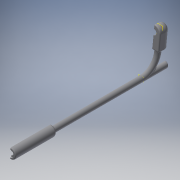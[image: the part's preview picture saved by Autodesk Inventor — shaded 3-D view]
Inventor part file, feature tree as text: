
AUTODESK INVENTOR PART (.ipt)
format: ipt  version: 2018 (Build 220112000, 112)  size: 352,256 bytes
history: native  units: mm
features: sketch x9, extrude x7, fillet x5, projected_geometry x3, plane x2, revolve x1, sweep x1
ambient origin geometry x8: Origin, YZ Plane, XZ Plane, XY Plane, X Axis, Y Axis, Z Axis, Center Point
bodies: Solid1 (feature_tree)
feature tree (28):
  revolve  "Revolution1"  [1 undecoded]
  fillet  "Fillet1"  Radius=8.0mm
  fillet  "Fillet2"  Radius=40.0mm
  fillet  "Fillet3"  [1 undecoded]
  plane  "Work Plane1"
  sweep  "Sweep1"
  extrude  "Extrusion2"  Depth=1.5mm
  fillet  "Fillet4"  Radius=1.0mm
  fillet  "Fillet5"  Radius=1.0mm
  extrude  "Extrusion3"  Depth=1.0mm
  extrude  "Extrusion4"  Depth=6.601018mm
  extrude  "Extrusion5"  Depth=1.0mm
  extrude  "Extrusion6"  [1 undecoded]
  extrude  "Extrusion7"  Depth=18.0mm
  plane  "Work Plane3"
  extrude  "Extrusion8"  TaperAngle=0.0deg  [1 undecoded]
  sketch  "Sketch6"  dims[d0=150.0mm d1=3.0mm d3=8.0mm d4=40.0mm d5=90.0deg]
  sketch  "Sketch8"  dims[d20=1.5mm d21=1.5mm]
  sketch  "Sketch9"  dims[d22=1.5mm d23=1.0mm d24=1.0mm d25=1.0mm]
  projected_geometry  "Projected Loop3"
  sketch  "Sketch10"  dims[d26=1.0mm d27=1.0mm]
  projected_geometry  "Projected Loop4"
  sketch  "Sketch11"  dims[d28=1.456552mm d29=6.601018mm]
  sketch  "Sketch12"  dims[d30=2.0mm d31=1.0mm]
  sketch  "Sketch13"  dims[d32=1.0mm d33=-23.0mm]
  sketch  "Sketch14"  dims[d38=18.0mm d39=18.0mm]
  sketch  "Sketch15"  dims[d40=16.0mm d41=0.0mm d42=0.0mm d43=12.0mm d44=5.0mm d45=6.0mm d46=6.0mm d47=20.0mm d48=0.0mm d49=6.0mm d50=1.0mm d51=3.0mm d52=5.0mm d53=8.0mm d54=0.0mm d55=10.0mm d56=0.0mm d57=50.0mm d58=0.0mm d59=1.4mm d60=0.0mm d61=4.332171mm d62=15.0mm d63=0.0mm d64=-3.0mm d65=6.0mm d66=1.1mm d67=0.0mm]
  projected_geometry  "Projected Loop5"
note: 4 required parameter values undecoded (feature->parameter linkage not recoverable at this tier; creation-order binding heuristic only, values carry confidence <= 0.55)